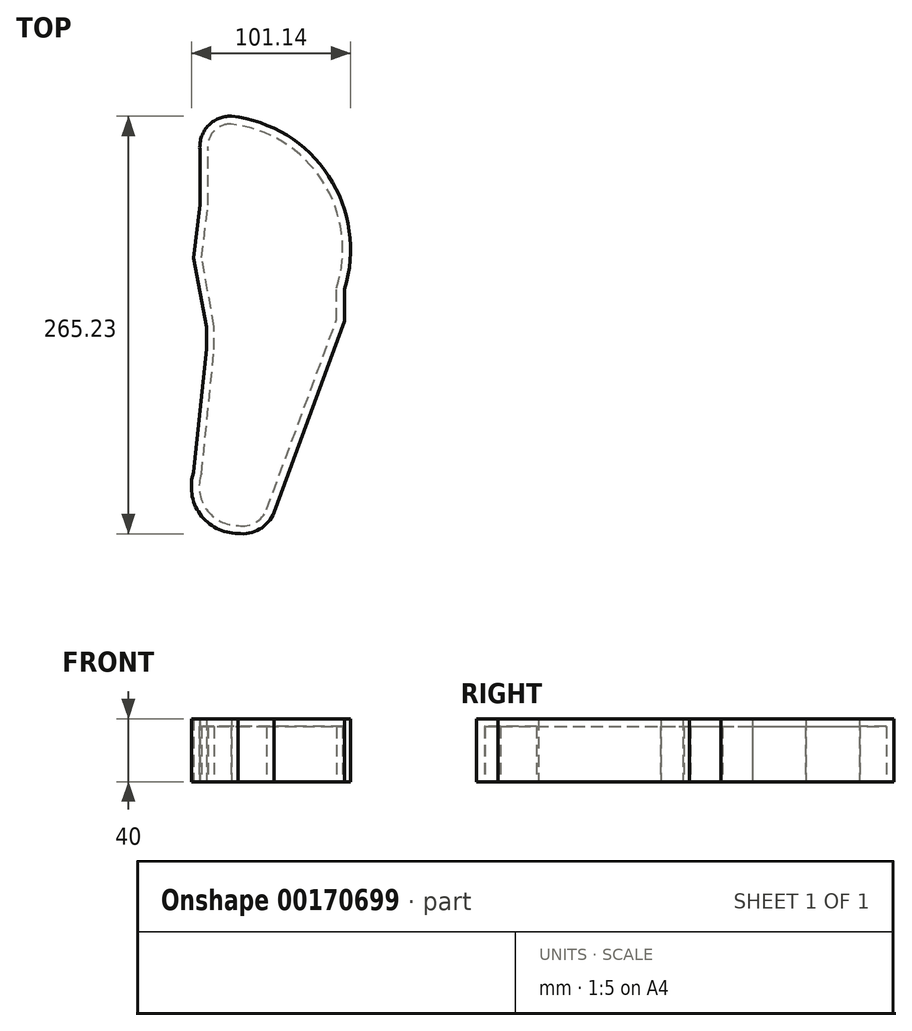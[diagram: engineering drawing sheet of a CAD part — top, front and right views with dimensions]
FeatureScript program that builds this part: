
annotation { "Feature Type Name" : "Feature", "Feature Type Description" : "" }
export const myFeature = defineFeature(function(context is Context, id is Id, definition is map)
    precondition{}
    {
        {
            var Q0;
            Q0=qCreatedBy(makeId("Top.planeOp"),FACE);
            var sketch = newSketch(context, id + "F0", { "sketchPlane" : qUnion([Q0])});
            skArc(sketch, "E0", {"start": v(-28, 39) * mm, "mid": v(-24, 12.32) * mm, "end": v(0, 0) * mm});
            skLineSegment(sketch, "E1", {"start": v(-28, 39) * mm, "end": v(-20, 117) * mm});
            skLineSegment(sketch, "E2", {"start": v(-20, 117) * mm, "end": v(-20, 131) * mm});
            skLineSegment(sketch, "E3", {"start": v(-20, 131) * mm, "end": v(-28, 175) * mm});
            skLineSegment(sketch, "E4", {"start": v(-28, 175) * mm, "end": v(-24, 209) * mm});
            skLineSegment(sketch, "E5", {"start": v(-24, 209) * mm, "end": v(-24, 243) * mm});
            skArc(sketch, "E6", {"start": v(-4, 265) * mm, "mid": v(-19.1, 258.64) * mm, "end": v(-24, 243) * mm});
            skArc(sketch, "E7", {"start": v(0, 0) * mm, "mid": v(13.8, 2.66) * mm, "end": v(23, 13.3) * mm});
            skLineSegment(sketch, "E8", {"start": v(23, 13.3) * mm, "end": v(67.77, 134.88) * mm});
            skLineSegment(sketch, "E9", {"start": v(67.77, 134.88) * mm, "end": v(67.77, 155.1) * mm});
            skArc(sketch, "E10", {"start": v(67.77, 155.1) * mm, "mid": v(57.72, 226.92) * mm, "end": v(-4, 265) * mm});
            skSolve(sketch);
        }
        {
            var Q0;
            Q0 = qSketchRegion(id + "F0", true);
            extrude(context, id + "F1", {"entities" : qUnion([Q0]), "depth" : 40 * mm});
        }
        {
            var Q0;
            Q0=makeQuery(id+"F1.opExtrude","CAP_FACE",FACE,{"disambiguationData":[OSD([sQuery(id+"F0.wireOp",EDGE,"E0"),sQuery(id+"F0.wireOp",EDGE,"E1"),sQuery(id+"F0.wireOp",EDGE,"E2"),sQuery(id+"F0.wireOp",EDGE,"E3"),sQuery(id+"F0.wireOp",EDGE,"E4"),sQuery(id+"F0.wireOp",EDGE,"E5"),sQuery(id+"F0.wireOp",EDGE,"E6"),sQuery(id+"F0.wireOp",EDGE,"E7"),sQuery(id+"F0.wireOp",EDGE,"E8"),sQuery(id+"F0.wireOp",EDGE,"E9"),sQuery(id+"F0.wireOp",EDGE,"E10")])],"isStart":true});
            shell(context, id + "F2", {"entities" : qUnion([Q0]), "thickness" : 5 * mm});
        }
    });
